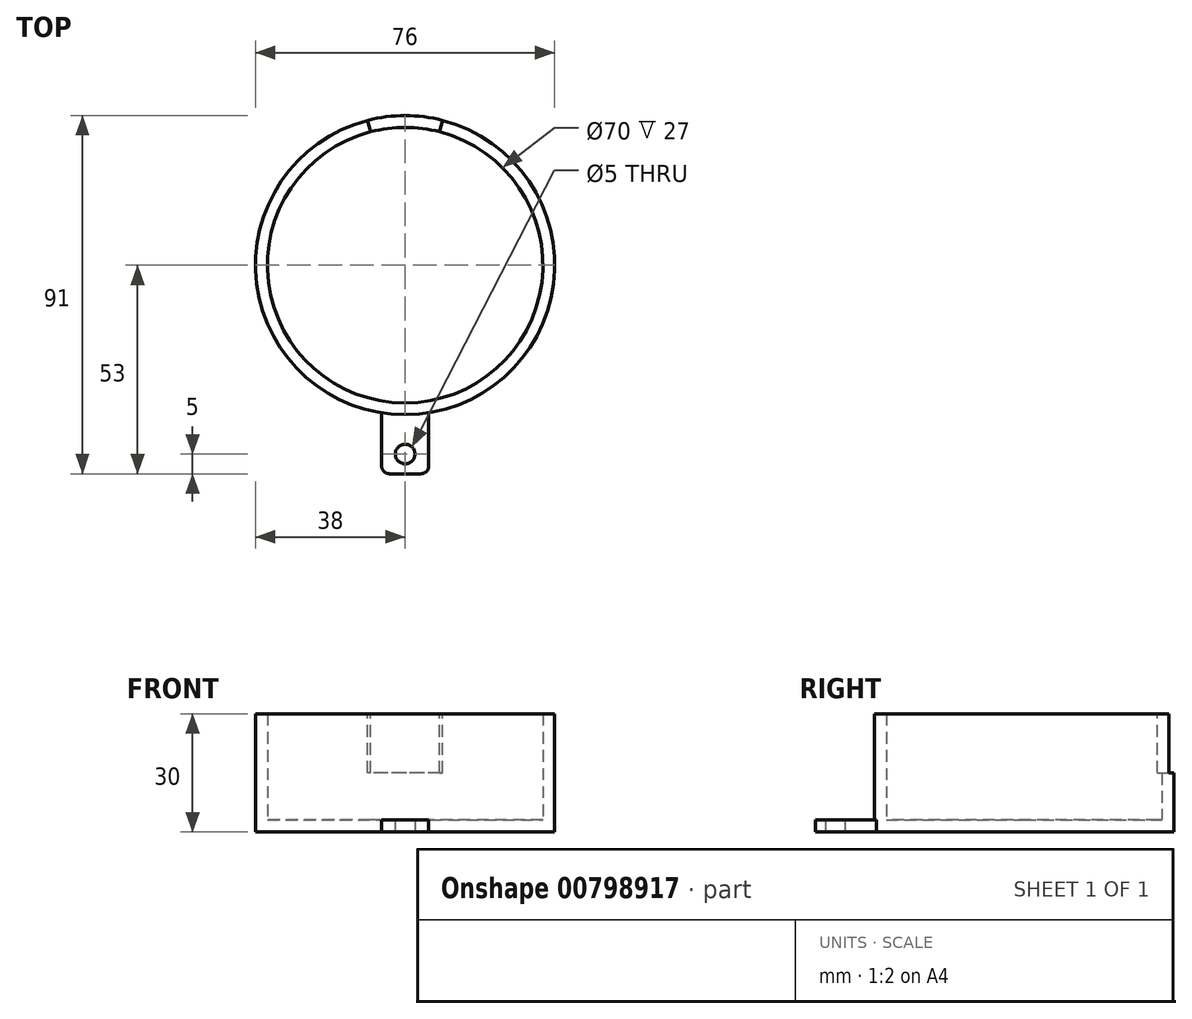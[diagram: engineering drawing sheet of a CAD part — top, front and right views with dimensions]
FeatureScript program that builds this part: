
annotation { "Feature Type Name" : "Feature", "Feature Type Description" : "" }
export const myFeature = defineFeature(function(context is Context, id is Id, definition is map)
    precondition{}
    {
        {
            var Q0;
            Q0=qCreatedBy(makeId("Top.planeOp"),FACE);
            var sketch = newSketch(context, id + "F0", { "sketchPlane" : qUnion([Q0])});
            skCircle(sketch, "E0", {"center": v(0, 0) * mm, "radius": 38 * mm});
            skSolve(sketch);
        }
        {
            var Q0;
            Q0 = qSketchRegion(id + "F0", true);
            extrude(context, id + "F1", {"entities" : qUnion([Q0]), "depth" : 3 * mm, "offsetDistance" : 25.4 * mm});
        }
        {
            var Q0;
            Q0=makeQuery(id+"F1.opExtrude","CAP_FACE",FACE,{"disambiguationData":[OSD([sQuery(id+"F0.wireOp",EDGE,"E0")])],"isStart":false});
            var sketch = newSketch(context, id + "F2", { "sketchPlane" : qUnion([Q0])});
            skCircle(sketch, "E1", {"center": v(0, 0) * mm, "radius": 38 * mm});
            skCircle(sketch, "E2", {"center": v(0, 0) * mm, "radius": 35 * mm});
            skSolve(sketch);
        }
        {
            var Q0;
            Q0 = qSketchRegion(id + "F2", true);
            extrude(context, id + "F3", {"entities" : qUnion([Q0]), "operationType" : NewBodyOperationType.ADD, "depth" : 27 * mm, "offsetDistance" : 25.4 * mm});
        }
        {
            var Q0;
            Q0=qCreatedBy(makeId("Top.planeOp"),FACE);
            var sketch = newSketch(context, id + "F4", { "sketchPlane" : qUnion([Q0])});
            skLineSegment(sketch, "E3.bottom", {"start": v(-6, -30) * mm, "end": v(6, -30) * mm});
            skLineSegment(sketch, "E3.top", {"start": v(-6, -53) * mm, "end": v(6, -53) * mm});
            skLineSegment(sketch, "E3.left", {"start": v(-6, -30) * mm, "end": v(-6, -53) * mm});
            skLineSegment(sketch, "E3.right", {"start": v(6, -30) * mm, "end": v(6, -53) * mm});
            skCircle(sketch, "E4", {"center": v(0, -48) * mm, "radius": 2.5 * mm});
            skSolve(sketch);
        }
        {
            var Q0;
            Q0=makeQuery(id+"F4.imprint","IMPRINT",FACE,{"disambiguationData":[TD([[makeQuery(id+"F4.imprint","IMPRINT",EDGE,{"derivedFrom":sQuery(id+"F4.wireOp",EDGE,"E3.bottom")}),-1.0]])]});
            extrude(context, id + "F5", {"entities" : qUnion([Q0]), "operationType" : NewBodyOperationType.ADD, "depth" : 3 * mm, "offsetDistance" : 25.4 * mm});
        }
        {
            var Q0;
            Q0=makeQuery(id+"F5.opExtrude","SWEPT_EDGE",EDGE,{"disambiguationData":[OSD([sQuery(id+"F4.wireOp",EDGE,"E3.top"),sQuery(id+"F4.wireOp",EDGE,"E3.right")])]});
            var Q1;
            Q1=makeQuery(id+"F5.opExtrude","SWEPT_EDGE",EDGE,{"disambiguationData":[OSD([sQuery(id+"F4.wireOp",EDGE,"E3.top"),sQuery(id+"F4.wireOp",EDGE,"E3.left")])]});
            fillet(context, id + "F6", {"entities" : qUnion([Q0, Q1]), "radius" : 2 * mm, "tangentPropagation" : true, "allowEdgeOverflow" : false});
        }
        {
            var Q0;
            Q0=makeQuery(id+"F3.opExtrude","CAP_FACE",FACE,{"disambiguationData":[OSD([sQuery(id+"F2.wireOp",EDGE,"E1"),sQuery(id+"F2.wireOp",EDGE,"E2")])],"isStart":false});
            var sketch = newSketch(context, id + "F7", { "sketchPlane" : qUnion([Q0])});
            skLineSegment(sketch, "E5", {"start": v(0, 0) * mm, "end": v(-10.02, 38.73) * mm});
            skLineSegment(sketch, "E6", {"start": v(0, 0) * mm, "end": v(10.1, 39.04) * mm});
            skArc(sketch, "E7", {"start": v(-10.02, 38.73) * mm, "mid": v(0, 40) * mm, "end": v(10.02, 38.73) * mm});
            skSolve(sketch);
        }
        {
            var Q0;
            {var subQ0=sQuery(id+"F7.wireOp",EDGE,"E5");var subQ1=makeQuery(id+"F3.opExtrude","CAP_EDGE",EDGE,{"disambiguationData":[OSD([sQuery(id+"F2.wireOp",EDGE,"E1")])],"isStart":false});var subQ2=makeQuery(id+"F7.imprint","INTERSECT",VERTEX,{"derivedFrom":[subQ1,subQ0]});Q0=makeQuery(id+"F7.imprint","IMPRINT",FACE,{"disambiguationData":[TD([[makeQuery(id+"F7.imprint","IMPRINT",EDGE,{"disambiguationData":[TD([[subQ2,1.0]])],"derivedFrom":subQ0}),-1.0]])]});}
            extrude(context, id + "F8", {"entities" : qUnion([Q0]), "operationType" : NewBodyOperationType.REMOVE, "oppositeDirection" : true, "depth" : 15 * mm, "offsetDistance" : 25.4 * mm});
        }
    });
